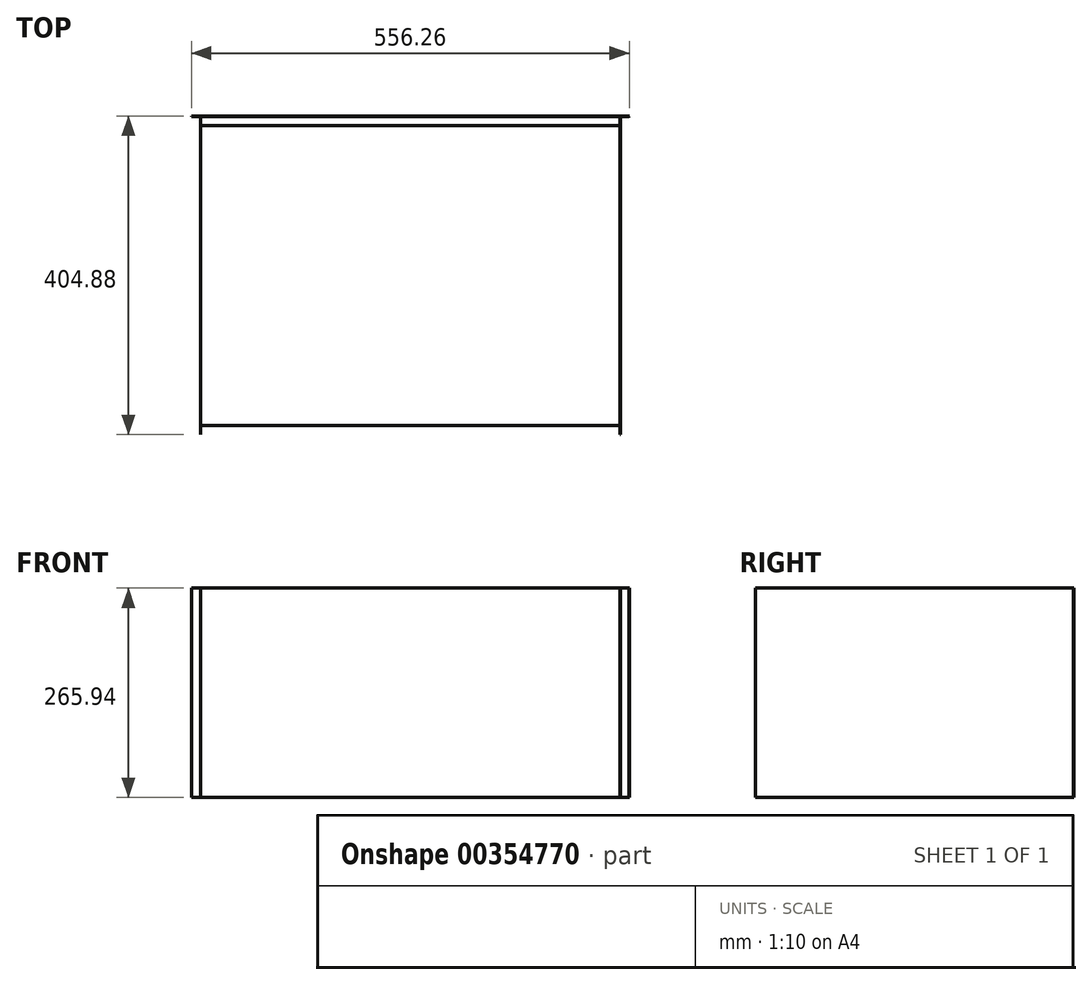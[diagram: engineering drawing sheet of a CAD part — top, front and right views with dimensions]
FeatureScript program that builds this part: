
annotation { "Feature Type Name" : "Feature", "Feature Type Description" : "" }
export const myFeature = defineFeature(function(context is Context, id is Id, definition is map)
    precondition{}
    {
        {
            assignVariable(context, id + "F0", {"name" : "Thk", "anyValue" : .47});
        }
        {
            var Q0;
            Q0=qCreatedBy(makeId("Front.planeOp"),FACE);
            var sketch = newSketch(context, id + "F1", { "sketchPlane" : qUnion([Q0])});
            skLineSegment(sketch, "E0.bottom", {"start": v(-278.13, 0) * mm, "end": v(278.13, 0) * mm});
            skLineSegment(sketch, "E0.top", {"start": v(-278.13, 265.94) * mm, "end": v(278.13, 265.94) * mm});
            skLineSegment(sketch, "E0.left", {"start": v(-278.13, 0) * mm, "end": v(-278.13, 265.94) * mm});
            skLineSegment(sketch, "E0.right", {"start": v(278.13, 0) * mm, "end": v(278.13, 265.94) * mm});
            skPoint(sketch, "E0.middle", {"position": v(0, 132.97) * mm});
            skSolve(sketch);
        }
        {
            var Q0;
            Q0=makeQuery(id+"F1.imprint","IMPRINT",FACE,{"disambiguationData":[TD([[makeQuery(id+"F1.imprint","IMPRINT",EDGE,{"derivedFrom":sQuery(id+"F1.wireOp",EDGE,"E0.bottom")}),1.0]])]});
            extrude(context, id + "F2", {"entities" : qUnion([Q0]), "depth" : (getVariable(context, 'Thk')) * mm});
        }
        {
            var Q0;
            Q0=makeQuery(id+"F2.opExtrude","SWEPT_FACE",FACE,{"disambiguationData":[OSD([sQuery(id+"F1.wireOp",EDGE,"E0.bottom")])]});
            var sketch = newSketch(context, id + "F3", { "sketchPlane" : qUnion([Q0])});
            skLineSegment(sketch, "E1.bottom", {"start": v(-266.2, 11.94) * mm, "end": v(266.2, 11.94) * mm});
            skLineSegment(sketch, "E1.top", {"start": v(-266.2, 392.94) * mm, "end": v(266.2, 392.94) * mm});
            skLineSegment(sketch, "E1.left", {"start": v(-266.2, 11.94) * mm, "end": v(-266.2, 392.94) * mm});
            skLineSegment(sketch, "E1.right", {"start": v(266.2, 11.94) * mm, "end": v(266.2, 392.94) * mm});
            skPoint(sketch, "E2.orphan", {"position": v(278.13, 392.94) * mm});
            skSolve(sketch);
        }
        {
            var Q0;
            {var subQ0=sQuery(id+"F3.wireOp",EDGE,"E1.top");Q0=makeQuery(id+"F3.imprint","IMPRINT",FACE,{"disambiguationData":[TD([[makeQuery(id+"F3.imprint","IMPRINT",EDGE,{"derivedFrom":subQ0}),-1.0]])]});}
            var Q1;
            {var subQ0=sQuery(id+"F3.wireOp",EDGE,"E1.bottom");Q1=makeQuery(id+"F3.imprint","IMPRINT",FACE,{"disambiguationData":[TD([[makeQuery(id+"F3.imprint","IMPRINT",EDGE,{"derivedFrom":subQ0}),1.0]])]});}
            extrude(context, id + "F4", {"entities" : qUnion([Q0, Q1]), "oppositeDirection" : true, "depth" : (getVariable(context, 'Thk')) * mm});
        }
        {
            var Q0;
            Q0=makeQuery(id+"F4.opExtrude","SWEPT_FACE",FACE,{"disambiguationData":[OSD([sQuery(id+"F3.wireOp",EDGE,"E1.left")])]});
            var sketch = newSketch(context, id + "F5", { "sketchPlane" : qUnion([Q0])});
            skLineSegment(sketch, "E3.bottom", {"start": v(0, 0) * mm, "end": v(404.88, 0) * mm});
            skLineSegment(sketch, "E3.top", {"start": v(0, 265.94) * mm, "end": v(404.88, 265.94) * mm});
            skLineSegment(sketch, "E3.left", {"start": v(0, 0) * mm, "end": v(0, 265.94) * mm});
            skLineSegment(sketch, "E3.right", {"start": v(404.88, 0) * mm, "end": v(404.88, 265.94) * mm});
            skSolve(sketch);
        }
        {
            var Q0;
            Q0=qSketchRegion(id+"F5",true);
            extrude(context, id + "F6", {"entities" : qUnion([Q0]), "depth" : (getVariable(context, 'Thk')) * mm});
        }
        {
            var Q0;
            Q0=makeQuery(id+"F6.opExtrude","SWEPT_BODY",BODY,{"disambiguationData":[OSD([sQuery(id+"F5.wireOp",EDGE,"E3.bottom"),sQuery(id+"F5.wireOp",EDGE,"E3.top"),sQuery(id+"F5.wireOp",EDGE,"E3.left"),sQuery(id+"F5.wireOp",EDGE,"E3.right")])]});
            var Q1;
            Q1=qCreatedBy(makeId("Right.planeOp"),FACE);
            mirror(context, id + "F7", {"entities" : qUnion([Q0]), "mirrorPlane" : qUnion([Q1])});
        }
        {
            var Q0;
            Q0=makeQuery(id+"F2.opExtrude","CAP_EDGE",EDGE,{"disambiguationData":[OSD([sQuery(id+"F1.wireOp",EDGE,"E0.right")])],"isStart":false});
            var Q1;
            Q1=makeQuery(id+"F7.opPattern","COPY",EDGE,{"derivedFrom":makeQuery(id+"F6.opExtrude","CAP_EDGE",EDGE,{"disambiguationData":[OSD([sQuery(id+"F5.wireOp",EDGE,"E3.left")])],"isStart":true}),"instanceName":"1"});
            var Q2;
            Q2=makeQuery(id+"F6.opExtrude","CAP_EDGE",EDGE,{"disambiguationData":[OSD([sQuery(id+"F5.wireOp",EDGE,"E3.left")])],"isStart":true});
            var Q3;
            Q3=makeQuery(id+"F2.opExtrude","CAP_EDGE",EDGE,{"disambiguationData":[OSD([sQuery(id+"F1.wireOp",EDGE,"E0.left")])],"isStart":false});
            var Q4;
            Q4=makeQuery(id+"F7.opPattern","COPY",EDGE,{"derivedFrom":makeQuery(id+"F6.opExtrude","CAP_EDGE",EDGE,{"disambiguationData":[OSD([sQuery(id+"F5.wireOp",EDGE,"E3.right")])],"isStart":true}),"instanceName":"1"});
            var Q5;
            Q5=makeQuery(id+"F6.opExtrude","CAP_EDGE",EDGE,{"disambiguationData":[OSD([sQuery(id+"F5.wireOp",EDGE,"E3.right")])],"isStart":true});
            chamfer(context, id + "F8", {"entities" : qUnion([Q0, Q1, Q2, Q3, Q4, Q5]), "width" : (getVariable(context, 'Thk')) * mm, "tangentPropagation" : true});
        }
    });
